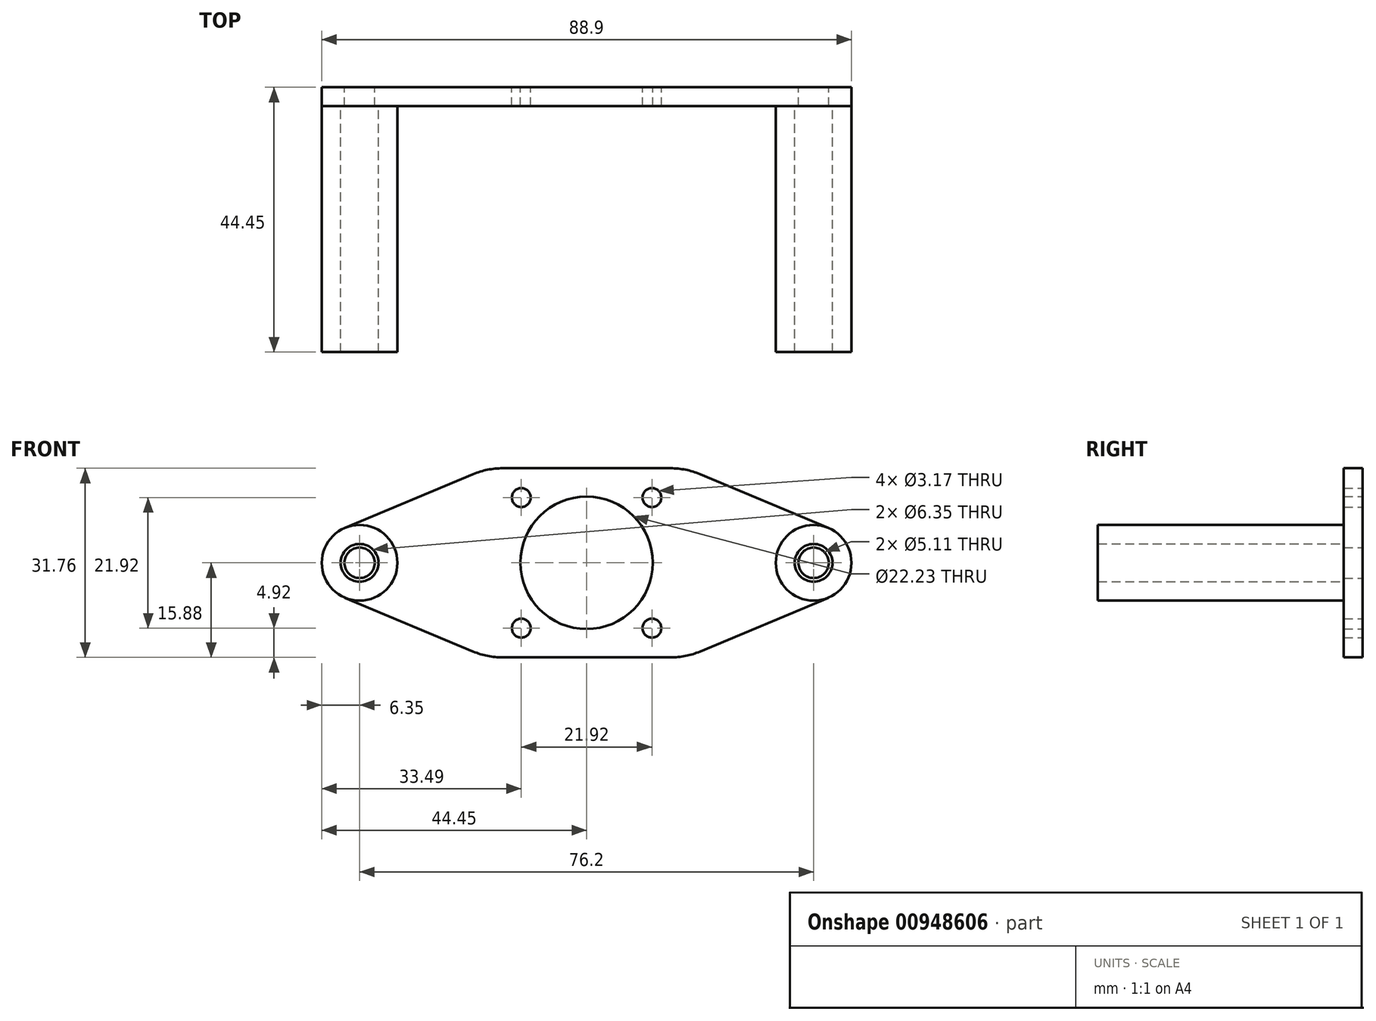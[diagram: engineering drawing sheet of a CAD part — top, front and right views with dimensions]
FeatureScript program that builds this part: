
annotation { "Feature Type Name" : "Feature", "Feature Type Description" : "" }
export const myFeature = defineFeature(function(context is Context, id is Id, definition is map)
    precondition{}
    {
        {
            var Q0;
            Q0=qCreatedBy(makeId("Front.planeOp"),FACE);
            var sketch = newSketch(context, id + "F0", { "sketchPlane" : qUnion([Q0])});
            skLineSegment(sketch, "E0", {"start": v(-38.1, 0) * mm, "end": v(0, 0) * mm, "construction": true});
            skLineSegment(sketch, "E1", {"start": v(38.1, 0) * mm, "end": v(0, 0) * mm, "construction": true});
            skCircle(sketch, "E2", {"center": v(-38.1, 0) * mm, "radius": 2.55 * mm});
            skCircle(sketch, "E3", {"center": v(38.1, 0) * mm, "radius": 2.55 * mm});
            skLineSegment(sketch, "E4.bottom", {"start": v(16.67, 15.88) * mm, "end": v(-16.67, 15.88) * mm, "construction": true});
            skLineSegment(sketch, "E4.top", {"start": v(16.67, -15.87) * mm, "end": v(-16.67, -15.88) * mm, "construction": true});
            skLineSegment(sketch, "E4.left", {"start": v(16.67, 15.88) * mm, "end": v(16.67, -15.88) * mm, "construction": true});
            skLineSegment(sketch, "E4.right", {"start": v(-16.67, 15.88) * mm, "end": v(-16.67, -15.88) * mm, "construction": true});
            skPoint(sketch, "E4.middle", {"position": v(0, 0) * mm});
            skLineSegment(sketch, "E5.bottom", {"start": v(10.96, 10.96) * mm, "end": v(-10.96, 10.96) * mm, "construction": true});
            skLineSegment(sketch, "E5.top", {"start": v(10.96, -10.96) * mm, "end": v(-10.96, -10.96) * mm, "construction": true});
            skLineSegment(sketch, "E5.left", {"start": v(10.96, 10.96) * mm, "end": v(10.96, -10.96) * mm, "construction": true});
            skLineSegment(sketch, "E5.right", {"start": v(-10.96, 10.96) * mm, "end": v(-10.96, -10.96) * mm, "construction": true});
            skCircle(sketch, "E6", {"center": v(10.96, 10.96) * mm, "radius": 1.59 * mm});
            skCircle(sketch, "E7", {"center": v(10.96, -10.96) * mm, "radius": 1.59 * mm});
            skCircle(sketch, "E8", {"center": v(-10.96, -10.96) * mm, "radius": 1.59 * mm});
            skCircle(sketch, "E9", {"center": v(-10.96, 10.96) * mm, "radius": 1.59 * mm});
            skArc(sketch, "E10", {"start": v(-40.56, 5.86) * mm, "mid": v(-44.45, 0) * mm, "end": v(-40.56, -5.86) * mm});
            skArc(sketch, "E11", {"start": v(40.56, 5.86) * mm, "mid": v(44.45, 0) * mm, "end": v(40.56, -5.86) * mm});
            skLineSegment(sketch, "E12", {"start": v(-40.56, 5.86) * mm, "end": v(-19.03, 14.89) * mm});
            skLineSegment(sketch, "E13", {"start": v(-40.56, -5.86) * mm, "end": v(-19.03, -14.89) * mm});
            skLineSegment(sketch, "E14", {"start": v(40.56, 5.86) * mm, "end": v(19.03, 14.89) * mm});
            skLineSegment(sketch, "E15", {"start": v(40.56, -5.86) * mm, "end": v(19.03, -14.89) * mm});
            skCircle(sketch, "E16", {"center": v(38.1, 0) * mm, "radius": 6.35 * mm, "construction": true});
            skCircle(sketch, "E17", {"center": v(-38.1, 0) * mm, "radius": 6.35 * mm, "construction": true});
            skLineSegment(sketch, "E18", {"start": v(-14.11, 15.88) * mm, "end": v(14.11, 15.88) * mm});
            skLineSegment(sketch, "E19", {"start": v(14.11, -15.87) * mm, "end": v(-14.11, -15.88) * mm});
            skPoint(sketch, "E20.visualSharp", {"position": v(-16.67, 15.88) * mm});
            skArc(sketch, "E20.filletArc", {"start": v(-14.11, 15.88) * mm, "mid": v(-16.62, 15.63) * mm, "end": v(-19.03, 14.89) * mm});
            skPoint(sketch, "E21.visualSharp", {"position": v(16.67, 15.88) * mm});
            skArc(sketch, "E21.filletArc", {"start": v(19.03, 14.89) * mm, "mid": v(16.62, 15.63) * mm, "end": v(14.11, 15.88) * mm});
            skPoint(sketch, "E22.visualSharp", {"position": v(16.67, -15.88) * mm});
            skArc(sketch, "E22.filletArc", {"start": v(14.11, -15.87) * mm, "mid": v(16.62, -15.63) * mm, "end": v(19.03, -14.89) * mm});
            skPoint(sketch, "E23.visualSharp", {"position": v(-16.67, -15.88) * mm});
            skArc(sketch, "E23.filletArc", {"start": v(-19.03, -14.89) * mm, "mid": v(-16.62, -15.63) * mm, "end": v(-14.11, -15.88) * mm});
            skCircle(sketch, "E24", {"center": v(0, 0) * mm, "radius": 11.11 * mm});
            skSolve(sketch);
        }
        {
            var Q0;
            Q0 = qSketchRegion(id + "F0", true);
            extrude(context, id + "F1", {"entities" : qUnion([Q0]), "depth" : 3.17 * mm, "offsetDistance" : 25.4 * mm});
        }
        {
            var Q0;
            Q0=makeQuery(id+"F1.opExtrude","CAP_FACE",FACE,{"disambiguationData":[OSD([sQuery(id+"F0.wireOp",EDGE,"E2"),sQuery(id+"F0.wireOp",EDGE,"E3"),sQuery(id+"F0.wireOp",EDGE,"E6"),sQuery(id+"F0.wireOp",EDGE,"E7"),sQuery(id+"F0.wireOp",EDGE,"E8"),sQuery(id+"F0.wireOp",EDGE,"E9"),sQuery(id+"F0.wireOp",EDGE,"E10"),sQuery(id+"F0.wireOp",EDGE,"E11"),sQuery(id+"F0.wireOp",EDGE,"E12"),sQuery(id+"F0.wireOp",EDGE,"E13"),sQuery(id+"F0.wireOp",EDGE,"E14"),sQuery(id+"F0.wireOp",EDGE,"E15"),sQuery(id+"F0.wireOp",EDGE,"E18"),sQuery(id+"F0.wireOp",EDGE,"E19"),sQuery(id+"F0.wireOp",EDGE,"E20.filletArc"),sQuery(id+"F0.wireOp",EDGE,"E21.filletArc"),sQuery(id+"F0.wireOp",EDGE,"E22.filletArc"),sQuery(id+"F0.wireOp",EDGE,"E23.filletArc"),sQuery(id+"F0.wireOp",EDGE,"E24")])],"isStart":false});
            var sketch = newSketch(context, id + "F2", { "sketchPlane" : qUnion([Q0])});
            skCircle(sketch, "E25", {"center": v(-38.1, 0) * mm, "radius": 6.35 * mm});
            skCircle(sketch, "E26", {"center": v(38.1, 0) * mm, "radius": 6.35 * mm});
            skCircle(sketch, "E27", {"center": v(-38.1, 0) * mm, "radius": 3.18 * mm});
            skCircle(sketch, "E28", {"center": v(38.1, 0) * mm, "radius": 3.18 * mm});
            skSolve(sketch);
        }
        {
            var Q0;
            Q0 = qSketchRegion(id + "F2", true);
            extrude(context, id + "F3", {"entities" : qUnion([Q0]), "depth" : 41.27 * mm, "offsetDistance" : 25.4 * mm});
        }
    });
